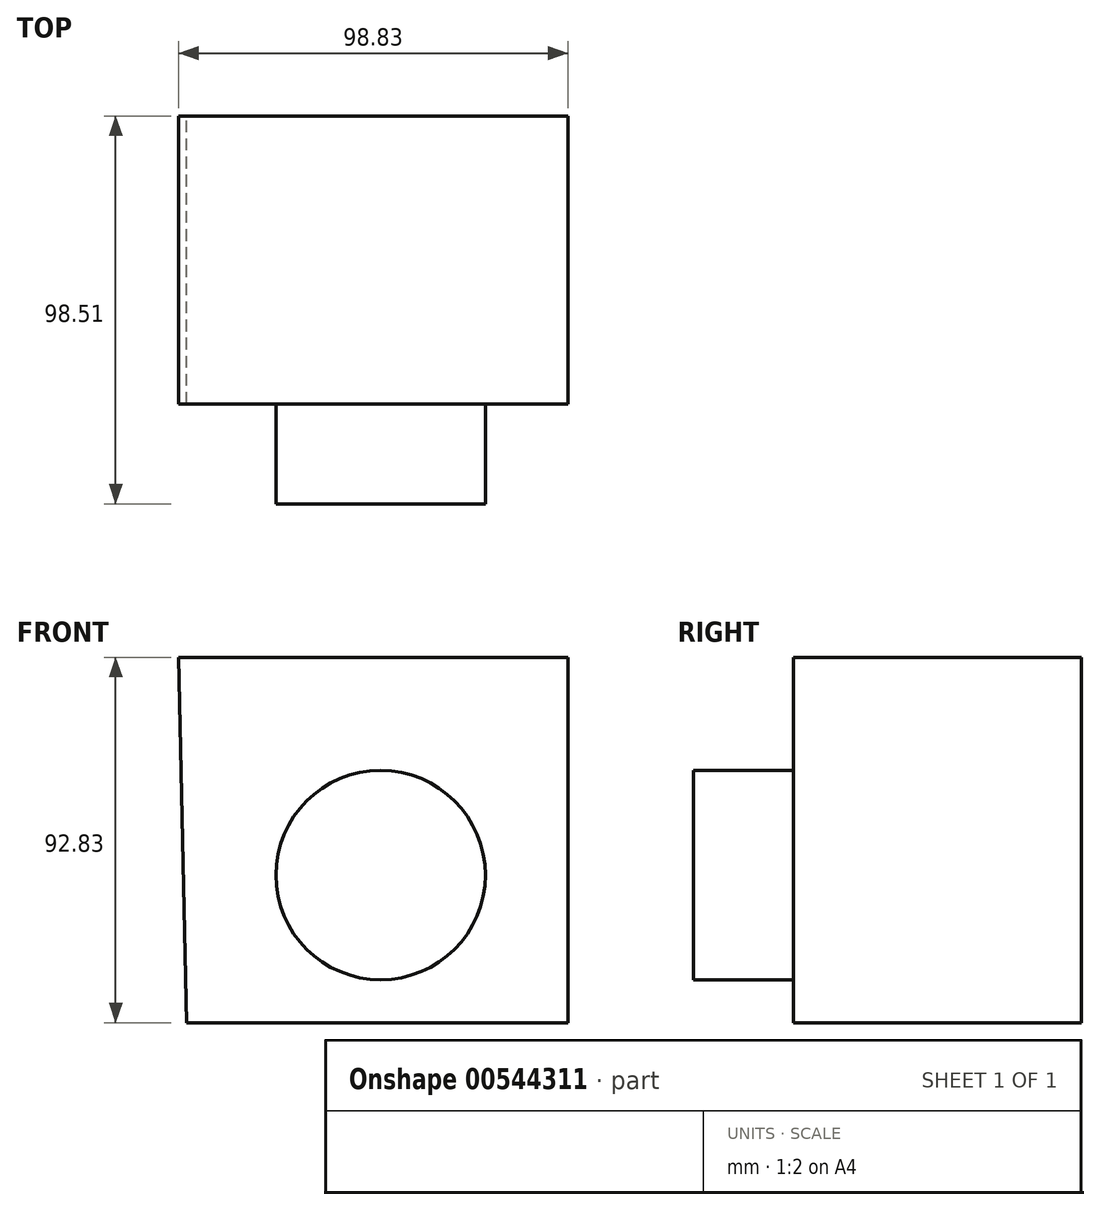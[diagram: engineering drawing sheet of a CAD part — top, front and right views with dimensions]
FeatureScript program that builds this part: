
annotation { "Feature Type Name" : "Feature", "Feature Type Description" : "" }
export const myFeature = defineFeature(function(context is Context, id is Id, definition is map)
    precondition{}
    {
        {
            var Q0;
            Q0=qCreatedBy(makeId("Front.planeOp"),FACE);
            var sketch = newSketch(context, id + "F0", { "sketchPlane" : qUnion([Q0])});
            skLineSegment(sketch, "E0", {"start": v(-49.34, -37.5) * mm, "end": v(47.54, -37.5) * mm});
            skLineSegment(sketch, "E1", {"start": v(47.54, -37.5) * mm, "end": v(47.54, 55.34) * mm});
            skLineSegment(sketch, "E2", {"start": v(47.54, 55.34) * mm, "end": v(-51.3, 55.34) * mm});
            skLineSegment(sketch, "E3", {"start": v(-51.3, 55.34) * mm, "end": v(-49.34, -37.5) * mm});
            skSolve(sketch);
        }
        {
            var Q0;
            Q0=makeQuery(id+"F0.imprint","IMPRINT",FACE,{"disambiguationData":[TD([[makeQuery(id+"F0.imprint","IMPRINT",EDGE,{"derivedFrom":sQuery(id+"F0.wireOp",EDGE,"E0")}),1.0]])]});
            extrude(context, id + "F1", {"entities" : qUnion([Q0]), "depth" : 73.11 * mm, "offsetDistance" : 25.4 * mm});
        }
        {
            var Q0;
            Q0=makeQuery(id+"F1.opExtrude","CAP_FACE",FACE,{"disambiguationData":[OSD([sQuery(id+"F0.wireOp",EDGE,"E0"),sQuery(id+"F0.wireOp",EDGE,"E1"),sQuery(id+"F0.wireOp",EDGE,"E2"),sQuery(id+"F0.wireOp",EDGE,"E3")])],"isStart":false});
            var sketch = newSketch(context, id + "F2", { "sketchPlane" : qUnion([Q0])});
            skCircle(sketch, "E4", {"center": v(0, 0) * mm, "radius": 26.6 * mm});
            skSolve(sketch);
        }
        {
            var Q0;
            Q0=makeQuery(id+"F2.imprint","IMPRINT",FACE,{"disambiguationData":[TD([[makeQuery(id+"F2.imprint","IMPRINT",EDGE,{"derivedFrom":sQuery(id+"F2.wireOp",EDGE,"E4")}),1.0]])]});
            extrude(context, id + "F3", {"entities" : qUnion([Q0]), "operationType" : NewBodyOperationType.ADD, "depth" : 25.4 * mm, "offsetDistance" : 25.4 * mm});
        }
        {
            var Q0;
            Q0=makeQuery(id+"F3.opExtrude","CAP_FACE",FACE,{"disambiguationData":[OSD([sQuery(id+"F2.wireOp",EDGE,"E4")])],"isStart":false});
            var sketch = newSketch(context, id + "F4", { "sketchPlane" : qUnion([Q0])});
            skCircle(sketch, "E5", {"center": v(0, 20.18) * mm, "radius": 6.43 * mm});
            skSolve(sketch);
        }
        {
            var Q0;
            Q0=sQuery(id+"F4.wireOp",EDGE,"E5");
            extrude(context, id + "F5", {"bodyType" : ToolBodyType.SURFACE, "surfaceEntities" : qUnion([Q0]), "depth" : 25.4 * mm, "offsetDistance" : 25.4 * mm});
        }
    });
